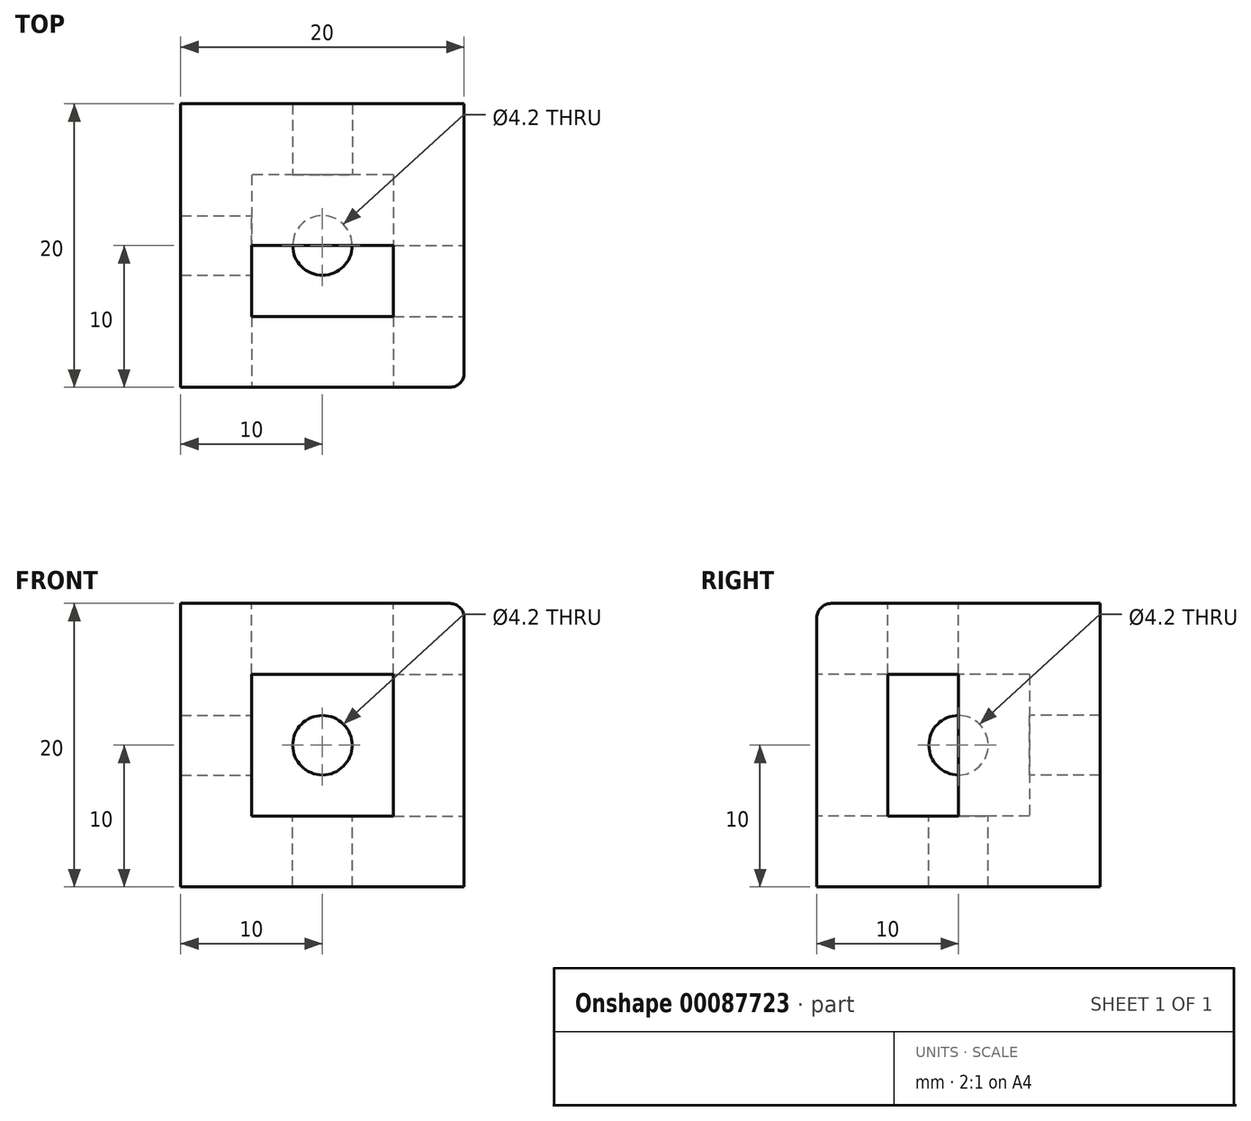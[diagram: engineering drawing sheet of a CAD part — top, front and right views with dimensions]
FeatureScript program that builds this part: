
annotation { "Feature Type Name" : "Feature", "Feature Type Description" : "" }
export const myFeature = defineFeature(function(context is Context, id is Id, definition is map)
    precondition{}
    {
        {
            var Q0;
            Q0=qCreatedBy(makeId("Front.planeOp"),FACE);
            var sketch = newSketch(context, id + "F0", { "sketchPlane" : qUnion([Q0])});
            skLineSegment(sketch, "E0.bottom", {"start": v(0, 0) * mm, "end": v(20, 0) * mm});
            skLineSegment(sketch, "E0.top", {"start": v(0, 20) * mm, "end": v(20, 20) * mm});
            skLineSegment(sketch, "E0.left", {"start": v(0, 0) * mm, "end": v(0, 20) * mm});
            skLineSegment(sketch, "E0.right", {"start": v(20, 0) * mm, "end": v(20, 20) * mm});
            skSolve(sketch);
        }
        {
            var Q0;
            Q0=makeQuery(id+"F0.imprint","IMPRINT",FACE,{"disambiguationData":[TD([[makeQuery(id+"F0.imprint","IMPRINT",EDGE,{"derivedFrom":sQuery(id+"F0.wireOp",EDGE,"E0.bottom")}),1.0]])]});
            extrude(context, id + "F1", {"entities" : qUnion([Q0]), "depth" : 20 * mm});
        }
        {
            var Q0;
            Q0=makeQuery(id+"F1.opExtrude","CAP_FACE",FACE,{"disambiguationData":[OSD([sQuery(id+"F0.wireOp",EDGE,"E0.bottom"),sQuery(id+"F0.wireOp",EDGE,"E0.top"),sQuery(id+"F0.wireOp",EDGE,"E0.left"),sQuery(id+"F0.wireOp",EDGE,"E0.right")])],"isStart":false});
            var sketch = newSketch(context, id + "F2", { "sketchPlane" : qUnion([Q0])});
            skLineSegment(sketch, "E1", {"start": v(10, 20) * mm, "end": v(10, 0) * mm});
            skLineSegment(sketch, "E2", {"start": v(20, 10) * mm, "end": v(0, 10) * mm});
            skLineSegment(sketch, "E3.bottom", {"start": v(15, 15) * mm, "end": v(5, 15) * mm});
            skLineSegment(sketch, "E3.top", {"start": v(15, 5) * mm, "end": v(5, 5) * mm});
            skLineSegment(sketch, "E3.left", {"start": v(15, 15) * mm, "end": v(15, 5) * mm});
            skLineSegment(sketch, "E3.right", {"start": v(5, 15) * mm, "end": v(5, 5) * mm});
            skSolve(sketch);
        }
        {
            var Q0;
            {var subQ0=sQuery(id+"F2.wireOp",EDGE,"E3.bottom");var subQ1=sQuery(id+"F2.wireOp",EDGE,"E1");var subQ2=makeQuery(id+"F2.imprint","INTERSECT",VERTEX,{"derivedFrom":[subQ1,subQ0]});Q0=makeQuery(id+"F2.imprint","IMPRINT",FACE,{"disambiguationData":[TD([[makeQuery(id+"F2.imprint","IMPRINT",EDGE,{"disambiguationData":[TD([[subQ2,-1.0]])],"derivedFrom":subQ1}),-1.0]])]});}
            var Q1;
            {var subQ0=sQuery(id+"F2.wireOp",EDGE,"E3.bottom");var subQ1=sQuery(id+"F2.wireOp",EDGE,"E1");var subQ2=makeQuery(id+"F2.imprint","INTERSECT",VERTEX,{"derivedFrom":[subQ1,subQ0]});Q1=makeQuery(id+"F2.imprint","IMPRINT",FACE,{"disambiguationData":[TD([[makeQuery(id+"F2.imprint","IMPRINT",EDGE,{"disambiguationData":[TD([[subQ2,-1.0]])],"derivedFrom":subQ1}),1.0]])]});}
            var Q2;
            {var subQ0=sQuery(id+"F2.wireOp",EDGE,"E2");var subQ1=sQuery(id+"F2.wireOp",EDGE,"E1");var subQ2=makeQuery(id+"F2.imprint","INTERSECT",VERTEX,{"derivedFrom":[subQ1,subQ0]});Q2=makeQuery(id+"F2.imprint","IMPRINT",FACE,{"disambiguationData":[TD([[makeQuery(id+"F2.imprint","IMPRINT",EDGE,{"disambiguationData":[TD([[subQ2,-1.0]])],"derivedFrom":subQ1}),1.0]])]});}
            var Q3;
            {var subQ0=sQuery(id+"F2.wireOp",EDGE,"E2");var subQ1=sQuery(id+"F2.wireOp",EDGE,"E1");var subQ2=makeQuery(id+"F2.imprint","INTERSECT",VERTEX,{"derivedFrom":[subQ1,subQ0]});Q3=makeQuery(id+"F2.imprint","IMPRINT",FACE,{"disambiguationData":[TD([[makeQuery(id+"F2.imprint","IMPRINT",EDGE,{"disambiguationData":[TD([[subQ2,-1.0]])],"derivedFrom":subQ1}),-1.0]])]});}
            extrude(context, id + "F3", {"entities" : qUnion([Q0, Q1, Q2, Q3]), "operationType" : NewBodyOperationType.REMOVE, "oppositeDirection" : true, "depth" : 15 * mm});
        }
        {
            var Q0;
            Q0=makeQuery(id+"F3.boolean.opBoolean","COPY",FACE,{"derivedFrom":makeQuery(id+"F3.opExtrude","CAP_FACE",FACE,{"disambiguationData":[OSD([sQuery(id+"F2.wireOp",EDGE,"E3.bottom"),sQuery(id+"F2.wireOp",EDGE,"E3.top"),sQuery(id+"F2.wireOp",EDGE,"E3.left"),sQuery(id+"F2.wireOp",EDGE,"E3.right")])],"isStart":false})});
            var sketch = newSketch(context, id + "F4", { "sketchPlane" : qUnion([Q0])});
            skCircle(sketch, "E4", {"center": v(10, 10) * mm, "radius": 2.1 * mm});
            skPoint(sketch, "E4.centerSnap0", {"position": v(15, 10) * mm});
            skPoint(sketch, "E4.centerSnap1", {"position": v(10, 15) * mm});
            skSolve(sketch);
        }
        {
            var Q0;
            Q0=makeQuery(id+"F4.imprint","IMPRINT",FACE,{"disambiguationData":[TD([[makeQuery(id+"F4.imprint","IMPRINT",EDGE,{"derivedFrom":sQuery(id+"F4.wireOp",EDGE,"E4")}),1.0]])]});
            extrude(context, id + "F5", {"entities" : qUnion([Q0]), "operationType" : NewBodyOperationType.REMOVE, "oppositeDirection" : true, "depth" : 25 * mm});
        }
        {
            var Q0;
            Q0=makeQuery(id+"F1.opExtrude","SWEPT_FACE",FACE,{"disambiguationData":[OSD([sQuery(id+"F0.wireOp",EDGE,"E0.top")])]});
            var sketch = newSketch(context, id + "F6", { "sketchPlane" : qUnion([Q0])});
            skLineSegment(sketch, "E5", {"start": v(10, 0) * mm, "end": v(10, -20) * mm});
            skLineSegment(sketch, "E6", {"start": v(20, -10) * mm, "end": v(0, -10) * mm});
            skLineSegment(sketch, "E7", {"start": v(10, -10) * mm, "end": v(10, -5) * mm});
            skLineSegment(sketch, "E8", {"start": v(10, -5) * mm, "end": v(15, -5) * mm});
            skLineSegment(sketch, "E9.bottom", {"start": v(15, -5) * mm, "end": v(5, -5) * mm});
            skLineSegment(sketch, "E9.top", {"start": v(15, -15) * mm, "end": v(5, -15) * mm});
            skLineSegment(sketch, "E9.left", {"start": v(15, -5) * mm, "end": v(15, -15) * mm});
            skLineSegment(sketch, "E9.right", {"start": v(5, -5) * mm, "end": v(5, -15) * mm});
            skSolve(sketch);
        }
        {
            var Q0;
            {var subQ0=sQuery(id+"F6.wireOp",EDGE,"E7");Q0=makeQuery(id+"F6.imprint","IMPRINT",FACE,{"disambiguationData":[TD([[makeQuery(id+"F6.imprint","IMPRINT",EDGE,{"derivedFrom":subQ0}),1.0]])]});}
            var Q1;
            {var subQ0=sQuery(id+"F6.wireOp",EDGE,"E7");Q1=makeQuery(id+"F6.imprint","IMPRINT",FACE,{"disambiguationData":[TD([[makeQuery(id+"F6.imprint","IMPRINT",EDGE,{"derivedFrom":subQ0}),-1.0]])]});}
            var Q2;
            {var subQ3=sQuery(id+"F6.wireOp",EDGE,"E9.top");var subQ5=sQuery(id+"F6.wireOp",EDGE,"E9.left");var subQ7=makeQuery(id+"F6.imprint","INTERSECT",VERTEX,{"derivedFrom":[subQ3,subQ5]});Q2=makeQuery(id+"F6.imprint","IMPRINT",FACE,{"disambiguationData":[TD([[makeQuery(id+"F6.imprint","IMPRINT",EDGE,{"disambiguationData":[TD([[subQ7,-1.0]])],"derivedFrom":subQ3}),-1.0]])]});}
            var Q3;
            {var subQ3=sQuery(id+"F6.wireOp",EDGE,"E9.top");var subQ5=sQuery(id+"F6.wireOp",EDGE,"E9.right");var subQ7=makeQuery(id+"F6.imprint","INTERSECT",VERTEX,{"derivedFrom":[subQ3,subQ5]});Q3=makeQuery(id+"F6.imprint","IMPRINT",FACE,{"disambiguationData":[TD([[makeQuery(id+"F6.imprint","IMPRINT",EDGE,{"disambiguationData":[TD([[subQ7,1.0]])],"derivedFrom":subQ3}),-1.0]])]});}
            extrude(context, id + "F7", {"entities" : qUnion([Q0, Q1, Q2, Q3]), "operationType" : NewBodyOperationType.REMOVE, "oppositeDirection" : true, "depth" : 15 * mm});
        }
        {
            var Q0;
            Q0=makeQuery(id+"F3.boolean.opBoolean","COPY",FACE,{"derivedFrom":makeQuery(id+"F3.opExtrude","SWEPT_FACE",FACE,{"disambiguationData":[OSD([sQuery(id+"F2.wireOp",EDGE,"E3.top")])]})});
            var sketch = newSketch(context, id + "F8", { "sketchPlane" : qUnion([Q0])});
            skLineSegment(sketch, "E10", {"start": v(15, -5) * mm, "end": v(15, -15) * mm});
            skCircle(sketch, "E11", {"center": v(10, -10) * mm, "radius": 2.1 * mm});
            skPoint(sketch, "E11.centerSnap0", {"position": v(10, -5) * mm});
            skPoint(sketch, "E11.centerSnap1", {"position": v(15, -10) * mm});
            skSolve(sketch);
        }
        {
            var Q0;
            Q0=makeQuery(id+"F8.imprint","IMPRINT",FACE,{"disambiguationData":[TD([[makeQuery(id+"F8.imprint","IMPRINT",EDGE,{"derivedFrom":sQuery(id+"F8.wireOp",EDGE,"E11")}),1.0]])]});
            extrude(context, id + "F9", {"entities" : qUnion([Q0]), "operationType" : NewBodyOperationType.REMOVE, "oppositeDirection" : true, "depth" : 25 * mm});
        }
        {
            var Q0;
            Q0=makeQuery(id+"F1.opExtrude","SWEPT_FACE",FACE,{"disambiguationData":[OSD([sQuery(id+"F0.wireOp",EDGE,"E0.right")])]});
            var sketch = newSketch(context, id + "F10", { "sketchPlane" : qUnion([Q0])});
            skLineSegment(sketch, "E12", {"start": v(-10, 20) * mm, "end": v(-10, 0) * mm});
            skLineSegment(sketch, "E13", {"start": v(0, 10) * mm, "end": v(-20, 10) * mm});
            skLineSegment(sketch, "E14", {"start": v(-10, 10) * mm, "end": v(-5, 10) * mm});
            skLineSegment(sketch, "E15", {"start": v(-5, 10) * mm, "end": v(-5, 15) * mm});
            skLineSegment(sketch, "E16.bottom", {"start": v(-5, 15) * mm, "end": v(-15, 15) * mm});
            skLineSegment(sketch, "E16.top", {"start": v(-5, 5) * mm, "end": v(-15, 5) * mm});
            skLineSegment(sketch, "E16.left", {"start": v(-5, 15) * mm, "end": v(-5, 5) * mm});
            skLineSegment(sketch, "E16.right", {"start": v(-15, 15) * mm, "end": v(-15, 5) * mm});
            skSolve(sketch);
        }
        {
            var Q0;
            {var subQ3=sQuery(id+"F10.wireOp",EDGE,"E16.bottom");var subQ5=sQuery(id+"F10.wireOp",EDGE,"E16.right");var subQ7=makeQuery(id+"F10.imprint","INTERSECT",VERTEX,{"derivedFrom":[subQ3,subQ5]});Q0=makeQuery(id+"F10.imprint","IMPRINT",FACE,{"disambiguationData":[TD([[makeQuery(id+"F10.imprint","IMPRINT",EDGE,{"disambiguationData":[TD([[subQ7,1.0]])],"derivedFrom":subQ3}),1.0]])]});}
            var Q1;
            {var subQ0=sQuery(id+"F10.wireOp",EDGE,"E14");Q1=makeQuery(id+"F10.imprint","IMPRINT",FACE,{"disambiguationData":[TD([[makeQuery(id+"F10.imprint","IMPRINT",EDGE,{"derivedFrom":subQ0}),1.0]])]});}
            var Q2;
            {var subQ0=sQuery(id+"F10.wireOp",EDGE,"E14");Q2=makeQuery(id+"F10.imprint","IMPRINT",FACE,{"disambiguationData":[TD([[makeQuery(id+"F10.imprint","IMPRINT",EDGE,{"derivedFrom":subQ0}),-1.0]])]});}
            var Q3;
            {var subQ3=sQuery(id+"F10.wireOp",EDGE,"E16.top");var subQ5=sQuery(id+"F10.wireOp",EDGE,"E16.right");var subQ7=makeQuery(id+"F10.imprint","INTERSECT",VERTEX,{"derivedFrom":[subQ3,subQ5]});Q3=makeQuery(id+"F10.imprint","IMPRINT",FACE,{"disambiguationData":[TD([[makeQuery(id+"F10.imprint","IMPRINT",EDGE,{"disambiguationData":[TD([[subQ7,1.0]])],"derivedFrom":subQ3}),-1.0]])]});}
            extrude(context, id + "F11", {"entities" : qUnion([Q0, Q1, Q2, Q3]), "operationType" : NewBodyOperationType.REMOVE, "oppositeDirection" : true, "depth" : 15 * mm});
        }
        {
            var Q0;
            Q0=makeQuery(id+"F7.boolean.opBoolean","MERGE",FACE,{"derivedFrom":[makeQuery(id+"F3.boolean.opBoolean","COPY",FACE,{"derivedFrom":makeQuery(id+"F3.opExtrude","SWEPT_FACE",FACE,{"disambiguationData":[OSD([sQuery(id+"F2.wireOp",EDGE,"E3.right")])]})}),makeQuery(id+"F7.opExtrude","SWEPT_FACE",FACE,{"disambiguationData":[OSD([sQuery(id+"F6.wireOp",EDGE,"E9.right")])]})]});
            var sketch = newSketch(context, id + "F12", { "sketchPlane" : qUnion([Q0])});
            skLineSegment(sketch, "E17.bottom", {"start": v(-15, 15) * mm, "end": v(-5, 15) * mm});
            skLineSegment(sketch, "E17.top", {"start": v(-15, 5) * mm, "end": v(-5, 5) * mm});
            skLineSegment(sketch, "E17.left", {"start": v(-15, 15) * mm, "end": v(-15, 5) * mm});
            skLineSegment(sketch, "E17.right", {"start": v(-5, 15) * mm, "end": v(-5, 5) * mm});
            skCircle(sketch, "E18", {"center": v(-10, 10) * mm, "radius": 2.1 * mm});
            skPoint(sketch, "E18.centerSnap0", {"position": v(-5, 10) * mm});
            skPoint(sketch, "E18.centerSnap1", {"position": v(-10, 15) * mm});
            skSolve(sketch);
        }
        {
            var Q0;
            Q0=makeQuery(id+"F12.imprint","IMPRINT",FACE,{"disambiguationData":[TD([[makeQuery(id+"F12.imprint","IMPRINT",EDGE,{"derivedFrom":sQuery(id+"F12.wireOp",EDGE,"E18")}),1.0]])]});
            extrude(context, id + "F13", {"entities" : qUnion([Q0]), "operationType" : NewBodyOperationType.REMOVE, "oppositeDirection" : true, "depth" : 25 * mm});
        }
        {
            var Q0;
            Q0=makeQuery(id+"F1.opExtrude","SWEPT_EDGE",EDGE,{"disambiguationData":[OSD([sQuery(id+"F0.wireOp",EDGE,"E0.top"),sQuery(id+"F0.wireOp",EDGE,"E0.right")])]});
            var Q1;
            Q1=makeQuery(id+"F1.opExtrude","CAP_EDGE",EDGE,{"disambiguationData":[OSD([sQuery(id+"F0.wireOp",EDGE,"E0.top")])],"isStart":false});
            var Q2;
            Q2=makeQuery(id+"F1.opExtrude","CAP_EDGE",EDGE,{"disambiguationData":[OSD([sQuery(id+"F0.wireOp",EDGE,"E0.right")])],"isStart":false});
            fillet(context, id + "F14", {"entities" : qUnion([Q0, Q1, Q2]), "radius" : 1 * mm, "tangentPropagation" : true, "allowEdgeOverflow" : false});
        }
    });
